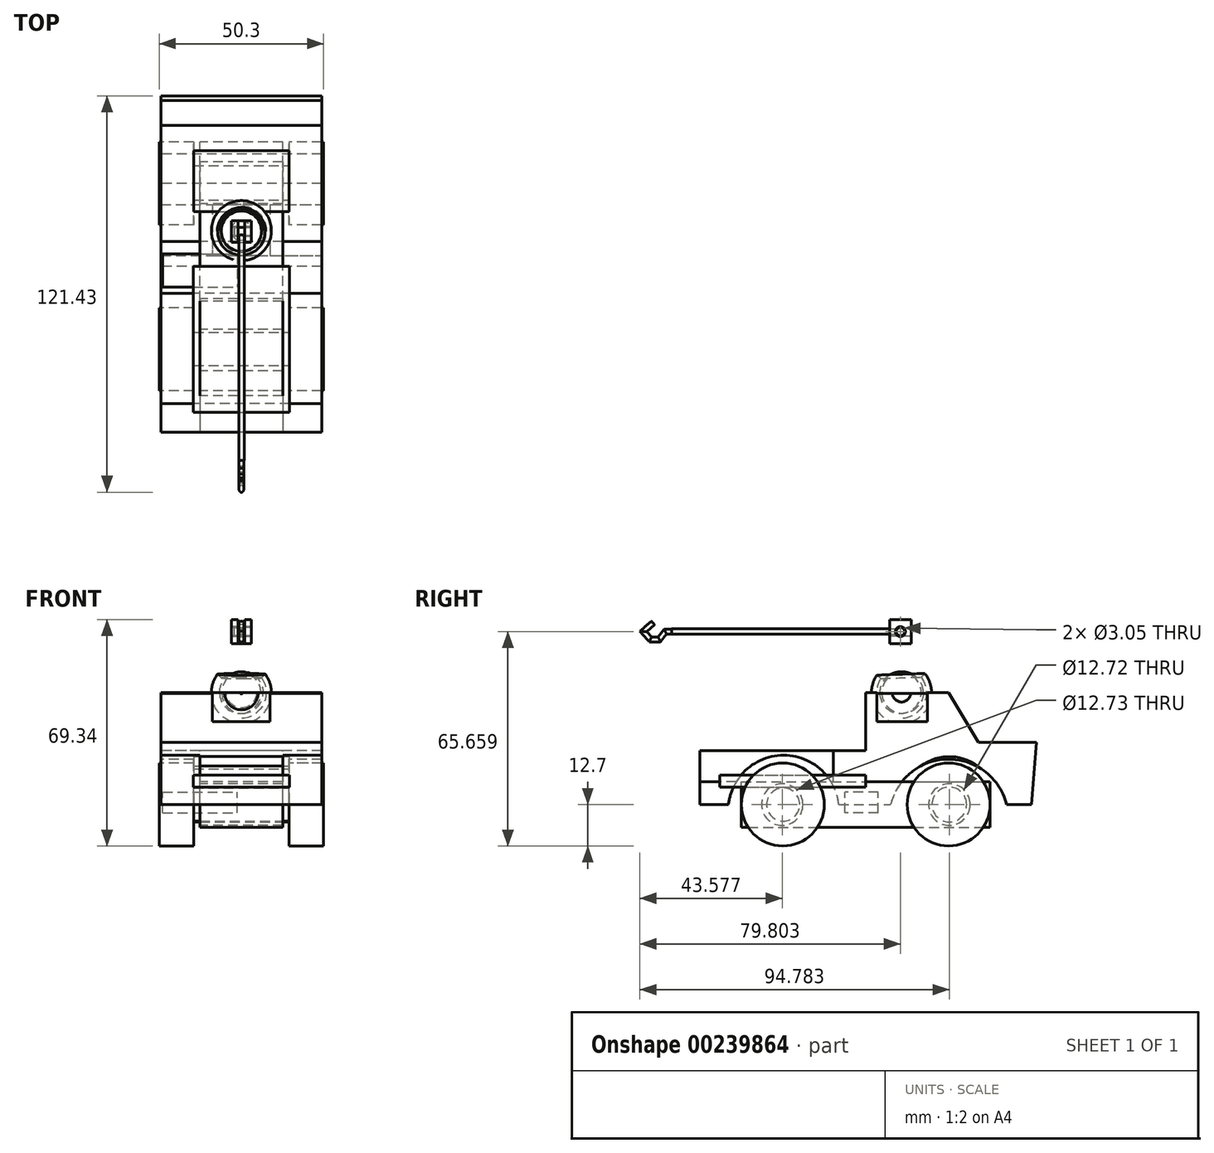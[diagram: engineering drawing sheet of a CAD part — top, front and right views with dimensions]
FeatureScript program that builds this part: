
annotation { "Feature Type Name" : "Feature", "Feature Type Description" : "" }
export const myFeature = defineFeature(function(context is Context, id is Id, definition is map)
    precondition{}
    {
        {
            var Q0;
            Q0=qCreatedBy(makeId("Right.planeOp"),FACE);
            var sketch = newSketch(context, id + "F0", { "sketchPlane" : qUnion([Q0])});
            skLineSegment(sketch, "E0", {"start": v(0, 0) * mm, "end": v(-50.8, 0) * mm, "construction": true});
            skLineSegment(sketch, "E1", {"start": v(0, 0) * mm, "end": v(50.8, 0) * mm, "construction": true});
            skCircle(sketch, "E2", {"center": v(-25.4, 0) * mm, "radius": 12.7 * mm});
            skCircle(sketch, "E3", {"center": v(25.4, 0) * mm, "radius": 12.7 * mm});
            skLineSegment(sketch, "E4", {"start": v(-42.06, 0) * mm, "end": v(-50.8, 0) * mm});
            skLineSegment(sketch, "E5", {"start": v(-50.8, 0) * mm, "end": v(-50.8, 16.51) * mm});
            skLineSegment(sketch, "E6", {"start": v(-50.8, 16.51) * mm, "end": v(0, 16.51) * mm});
            skLineSegment(sketch, "E7", {"start": v(0, 16.51) * mm, "end": v(0, 34.3) * mm});
            skLineSegment(sketch, "E8", {"start": v(0, 34.3) * mm, "end": v(25.4, 34.3) * mm});
            skLineSegment(sketch, "E9", {"start": v(25.4, 34.3) * mm, "end": v(34.47, 19) * mm});
            skLineSegment(sketch, "E10", {"start": v(34.47, 19) * mm, "end": v(52.25, 19) * mm});
            skLineSegment(sketch, "E11", {"start": v(52.25, 19) * mm, "end": v(50.8, 0) * mm});
            skArc(sketch, "E12", {"start": v(-8.23, 0) * mm, "mid": v(-25.15, 15.1) * mm, "end": v(-42.06, 0) * mm});
            skLineSegment(sketch, "E13", {"start": v(-8.23, 0) * mm, "end": v(7.62, 0) * mm});
            skArc(sketch, "E14", {"start": v(43.18, 0) * mm, "mid": v(25.4, 13.87) * mm, "end": v(7.62, 0) * mm});
            skLineSegment(sketch, "E15", {"start": v(43.18, 0) * mm, "end": v(50.8, 0) * mm});
            skSolve(sketch);
        }
        {
            var Q0;
            Q0=makeQuery(id+"F0.imprint","IMPRINT",FACE,{"disambiguationData":[TD([[makeQuery(id+"F0.imprint","IMPRINT",EDGE,{"derivedFrom":sQuery(id+"F0.wireOp",EDGE,"E4")}),-1.0]])]});
            extrude(context, id + "F1", {"entities" : qUnion([Q0]), "endBound" : BoundingType.SYMMETRIC, "depth" : 49.28 * mm});
        }
        {
            var Q0;
            Q0=makeQuery(id+"F0.imprint","IMPRINT",FACE,{"disambiguationData":[TD([[makeQuery(id+"F0.imprint","IMPRINT",EDGE,{"derivedFrom":sQuery(id+"F0.wireOp",EDGE,"E2")}),1.0]])]});
            var Q1;
            Q1=makeQuery(id+"F0.imprint","IMPRINT",FACE,{"disambiguationData":[TD([[makeQuery(id+"F0.imprint","IMPRINT",EDGE,{"derivedFrom":sQuery(id+"F0.wireOp",EDGE,"E3")}),1.0]])]});
            extrude(context, id + "F2", {"entities" : qUnion([Q0, Q1]), "endBound" : BoundingType.SYMMETRIC, "depth" : 50.3 * mm});
        }
        {
            var Q0;
            Q0=qCreatedBy(makeId("Right.planeOp"),FACE);
            var sketch = newSketch(context, id + "F3", { "sketchPlane" : qUnion([Q0])});
            skCircle(sketch, "E16", {"center": v(-25.3, 0) * mm, "radius": 14.08 * mm});
            skCircle(sketch, "E17", {"center": v(-25.3, 0) * mm, "radius": 5.07 * mm});
            skCircle(sketch, "E18", {"center": v(25.6, 0) * mm, "radius": 14.66 * mm});
            skCircle(sketch, "E19", {"center": v(25.6, 0) * mm, "radius": 5.32 * mm});
            skSolve(sketch);
        }
        {
            var Q0;
            Q0=makeQuery(id+"F3.imprint","IMPRINT",FACE,{"disambiguationData":[TD([[makeQuery(id+"F3.imprint","IMPRINT",EDGE,{"derivedFrom":sQuery(id+"F3.wireOp",EDGE,"E18")}),1.0]])]});
            extrude(context, id + "F4", {"entities" : qUnion([Q0]), "operationType" : NewBodyOperationType.REMOVE, "endBound" : BoundingType.SYMMETRIC, "oppositeDirection" : true, "depth" : 29.2 * mm});
        }
        {
            var Q0;
            Q0=makeQuery(id+"F3.imprint","IMPRINT",FACE,{"disambiguationData":[TD([[makeQuery(id+"F3.imprint","IMPRINT",EDGE,{"derivedFrom":sQuery(id+"F3.wireOp",EDGE,"E16")}),1.0]])]});
            extrude(context, id + "F5", {"entities" : qUnion([Q0]), "operationType" : NewBodyOperationType.REMOVE, "endBound" : BoundingType.SYMMETRIC, "oppositeDirection" : true, "depth" : 29.2 * mm});
        }
        {
            var Q0;
            Q0=makeQuery(id+"F1.opExtrude","SWEPT_FACE",FACE,{"disambiguationData":[OSD([sQuery(id+"F0.wireOp",EDGE,"E5")])]});
            var sketch = newSketch(context, id + "F6", { "sketchPlane" : qUnion([Q0])});
            skLineSegment(sketch, "E20.bottom", {"start": v(12.7, 6.99) * mm, "end": v(-12.7, 6.99) * mm});
            skLineSegment(sketch, "E20.top", {"start": v(12.7, 26.04) * mm, "end": v(-12.7, 26.04) * mm});
            skLineSegment(sketch, "E20.left", {"start": v(12.7, 6.99) * mm, "end": v(12.7, 26.04) * mm});
            skLineSegment(sketch, "E20.right", {"start": v(-12.7, 6.99) * mm, "end": v(-12.7, 26.04) * mm});
            skPoint(sketch, "E20.middle", {"position": v(0, 16.51) * mm});
            skSolve(sketch);
        }
        {
            var Q0;
            {var subQ0=sQuery(id+"F6.wireOp",EDGE,"E20.bottom");Q0=makeQuery(id+"F6.imprint","IMPRINT",FACE,{"disambiguationData":[TD([[makeQuery(id+"F6.imprint","IMPRINT",EDGE,{"derivedFrom":subQ0}),-1.0]])]});}
            extrude(context, id + "F7", {"entities" : qUnion([Q0]), "operationType" : NewBodyOperationType.REMOVE, "oppositeDirection" : true, "depth" : 40.9 * mm});
        }
        {
            var Q0;
            Q0=qCreatedBy(makeId("Front.planeOp"),FACE);
            var sketch = newSketch(context, id + "F8", { "sketchPlane" : qUnion([Q0])});
            skLineSegment(sketch, "E21.bottom", {"start": v(-14.78, 9) * mm, "end": v(14.78, 9) * mm});
            skLineSegment(sketch, "E21.top", {"start": v(-14.78, 5.33) * mm, "end": v(14.78, 5.33) * mm});
            skLineSegment(sketch, "E21.left", {"start": v(-14.78, 9) * mm, "end": v(-14.78, 5.33) * mm});
            skLineSegment(sketch, "E21.right", {"start": v(14.78, 9) * mm, "end": v(14.78, 5.33) * mm});
            skPoint(sketch, "E21.middle", {"position": v(0, 7.16) * mm});
            skSolve(sketch);
        }
        {
            var Q0;
            Q0 = qSketchRegion(id + "F8", true);
            extrude(context, id + "F9", {"entities" : qUnion([Q0]), "depth" : 44.7 * mm});
        }
        {
            var Q0;
            Q0=qCreatedBy(makeId("Right.planeOp"),FACE);
            var sketch = newSketch(context, id + "F10", { "sketchPlane" : qUnion([Q0])});
            skLineSegment(sketch, "E22.bottom", {"start": v(-38.1, -6.98) * mm, "end": v(38.1, -6.98) * mm});
            skLineSegment(sketch, "E22.top", {"start": v(-38.1, 6.98) * mm, "end": v(38.1, 6.98) * mm});
            skLineSegment(sketch, "E22.left", {"start": v(-38.1, -6.98) * mm, "end": v(-38.1, 6.98) * mm});
            skLineSegment(sketch, "E22.right", {"start": v(38.1, -6.98) * mm, "end": v(38.1, 6.98) * mm});
            skPoint(sketch, "E22.middle", {"position": v(0, 0) * mm});
            skCircle(sketch, "E23", {"center": v(25.6, 0) * mm, "radius": 6.36 * mm});
            skCircle(sketch, "E24", {"center": v(-25.6, 0) * mm, "radius": 6.36 * mm});
            skSolve(sketch);
        }
        {
            var Q0;
            Q0=makeQuery(id+"F10.imprint","IMPRINT",FACE,{"disambiguationData":[TD([[makeQuery(id+"F10.imprint","IMPRINT",EDGE,{"derivedFrom":sQuery(id+"F10.wireOp",EDGE,"E22.bottom")}),1.0]])]});
            extrude(context, id + "F11", {"entities" : qUnion([Q0]), "endBound" : BoundingType.SYMMETRIC, "depth" : 25.4 * mm});
        }
        {
            var Q0;
            Q0=qCreatedBy(makeId("Right.planeOp"),FACE);
            var sketch = newSketch(context, id + "F12", { "sketchPlane" : qUnion([Q0])});
            skCircle(sketch, "E25", {"center": v(11.28, 34.3) * mm, "radius": 9.53 * mm});
            skCircle(sketch, "E26", {"center": v(11.28, 34.3) * mm, "radius": 7.94 * mm});
            skCircle(sketch, "E27", {"center": v(11.28, 34.3) * mm, "radius": 6.35 * mm});
            skLineSegment(sketch, "E28", {"start": v(4.61, 38.6) * mm, "end": v(0, 42.52) * mm});
            skLineSegment(sketch, "E29", {"start": v(11.28, 34.3) * mm, "end": v(11.28, 27.94) * mm, "construction": true});
            skLineSegment(sketch, "E30", {"start": v(10.62, 43.8) * mm, "end": v(11.28, 24.77) * mm});
            skLineSegment(sketch, "E31.bottom", {"start": v(11.28, 34.3) * mm, "end": v(8.23, 34.3) * mm});
            skLineSegment(sketch, "E31.top", {"start": v(11.28, 49.53) * mm, "end": v(8.23, 49.53) * mm});
            skSolve(sketch);
        }
        {
            var Q0;
            Q0=makeQuery(id+"F1.opExtrude","CAP_FACE",FACE,{"disambiguationData":[OSD([sQuery(id+"F0.wireOp",EDGE,"E4"),sQuery(id+"F0.wireOp",EDGE,"E5"),sQuery(id+"F0.wireOp",EDGE,"E6"),sQuery(id+"F0.wireOp",EDGE,"E7"),sQuery(id+"F0.wireOp",EDGE,"E8"),sQuery(id+"F0.wireOp",EDGE,"E9"),sQuery(id+"F0.wireOp",EDGE,"E10"),sQuery(id+"F0.wireOp",EDGE,"E11"),sQuery(id+"F0.wireOp",EDGE,"E12"),sQuery(id+"F0.wireOp",EDGE,"E13"),sQuery(id+"F0.wireOp",EDGE,"E14"),sQuery(id+"F0.wireOp",EDGE,"E15")])],"isStart":false});
            var sketch = newSketch(context, id + "F13", { "sketchPlane" : qUnion([Q0])});
            skPoint(sketch, "E32.firstSnap0", {"position": v(0, 25.4) * mm});
            skLineSegment(sketch, "E32.bottom", {"start": v(3.35, 25.4) * mm, "end": v(18.9, 25.4) * mm});
            skLineSegment(sketch, "E32.top", {"start": v(3.35, 34.3) * mm, "end": v(18.9, 34.3) * mm});
            skLineSegment(sketch, "E32.left", {"start": v(3.35, 25.4) * mm, "end": v(3.35, 34.3) * mm});
            skLineSegment(sketch, "E32.right", {"start": v(18.9, 25.4) * mm, "end": v(18.9, 34.3) * mm});
            skSolve(sketch);
        }
        {
            var Q0;
            Q0=makeQuery(id+"F13.imprint","IMPRINT",FACE,{"disambiguationData":[TD([[makeQuery(id+"F13.imprint","IMPRINT",EDGE,{"derivedFrom":sQuery(id+"F13.wireOp",EDGE,"E32.bottom")}),1.0]])]});
            extrude(context, id + "F14", {"entities" : qUnion([Q0]), "operationType" : NewBodyOperationType.REMOVE, "oppositeDirection" : true, "depth" : 66.3 * mm});
        }
        {
            var Q0;
            {var subQ0=sQuery(id+"F12.wireOp",EDGE,"E30");var subQ1=sQuery(id+"F12.wireOp",EDGE,"E25");var subQ2=makeQuery(id+"F12.imprint","INTERSECT",VERTEX,{"disambiguationData":[OD(1.0)],"derivedFrom":[subQ1,subQ0]});Q0=makeQuery(id+"F12.imprint","IMPRINT",FACE,{"disambiguationData":[TD([[makeQuery(id+"F12.imprint","IMPRINT",EDGE,{"disambiguationData":[TD([[subQ2,1.0]])],"derivedFrom":subQ1}),1.0]])]});}
            var Q1;
            {var subQ0=sQuery(id+"F12.wireOp",EDGE,"E30");var subQ4=makeQuery(id+"F12.imprint","IMPRINT",VERTEX,{"derivedFrom":subQ0});Q1=makeQuery(id+"F12.imprint","IMPRINT",FACE,{"disambiguationData":[TD([[makeQuery(id+"F12.imprint","IMPRINT",EDGE,{"disambiguationData":[TD([[subQ4,1.0]])],"derivedFrom":subQ0}),-1.0]])]});}
            var Q2;
            Q2=sQuery(id+"F12.wireOp",EDGE,"E30");
            revolve(context, id + "F15", {"operationType" : NewBodyOperationType.ADD, "entities" : qUnion([Q0, Q1]), "axis" : qUnion([Q2]), "revolveType" : RevolveType.FULL});
        }
        {
            var Q0;
            Q0=qCreatedBy(makeId("Top.planeOp"),FACE);
            cPlane(context, id + "F16", {"entities" : qUnion([Q0]), "cplaneType" : CPlaneType.OFFSET, "offset" : 34.3 * mm, "width" : 152.4 * mm, "height" : 152.4 * mm});
        }
        {
            var Q0;
            Q0=qCreatedBy(id+"F16.planeOp",FACE);
            var sketch = newSketch(context, id + "F17", { "sketchPlane" : qUnion([Q0])});
            skCircle(sketch, "E33", {"center": v(0, 10.67) * mm, "radius": 2.6 * mm});
            skSolve(sketch);
        }
        {
            var Q0;
            Q0=sQuery(id+"F17.wireOp",EDGE,"E33");
            extrude(context, id + "F18", {"bodyType" : ToolBodyType.SURFACE, "surfaceEntities" : qUnion([Q0]), "depth" : 15.24 * mm});
        }
        {
            var Q0;
            Q0=qCreatedBy(id+"F16.planeOp",FACE);
            cPlane(context, id + "F19", {"entities" : qUnion([Q0]), "cplaneType" : CPlaneType.OFFSET, "offset" : 15 * mm, "width" : 152.4 * mm, "height" : 152.4 * mm});
        }
        {
            var Q0;
            Q0=qCreatedBy(id+"F19.planeOp",FACE);
            var sketch = newSketch(context, id + "F20", { "sketchPlane" : qUnion([Q0])});
            skLineSegment(sketch, "E34.bottom", {"start": v(-3.04, 13.92) * mm, "end": v(3.05, 13.92) * mm});
            skLineSegment(sketch, "E34.top", {"start": v(-3.04, 7.32) * mm, "end": v(3.05, 7.32) * mm});
            skLineSegment(sketch, "E34.left", {"start": v(-3.04, 13.92) * mm, "end": v(-3.04, 7.32) * mm});
            skLineSegment(sketch, "E34.right", {"start": v(3.05, 13.92) * mm, "end": v(3.05, 7.32) * mm});
            skLineSegment(sketch, "E35", {"start": v(-1.01, 13.92) * mm, "end": v(-1.01, 7.32) * mm});
            skLineSegment(sketch, "E36", {"start": v(1.02, 13.92) * mm, "end": v(1.02, 7.32) * mm});
            skSolve(sketch);
        }
        {
            var Q0;
            {var subQ0=sQuery(id+"F20.wireOp",EDGE,"E34.left");Q0=makeQuery(id+"F20.imprint","IMPRINT",FACE,{"disambiguationData":[TD([[makeQuery(id+"F20.imprint","IMPRINT",EDGE,{"derivedFrom":subQ0}),1.0]])]});}
            var Q1;
            {var subQ0=sQuery(id+"F20.wireOp",EDGE,"E34.right");Q1=makeQuery(id+"F20.imprint","IMPRINT",FACE,{"disambiguationData":[TD([[makeQuery(id+"F20.imprint","IMPRINT",EDGE,{"derivedFrom":subQ0}),-1.0]])]});}
            extrude(context, id + "F21", {"entities" : qUnion([Q0, Q1]), "depth" : 7.37 * mm});
        }
        {
            var Q0;
            Q0=makeQuery(id+"F21.opExtrude","SWEPT_FACE",FACE,{"disambiguationData":[OSD([sQuery(id+"F20.wireOp",EDGE,"E34.left")])]});
            var sketch = newSketch(context, id + "F22", { "sketchPlane" : qUnion([Q0])});
            skCircle(sketch, "E37", {"center": v(-10.62, 52.96) * mm, "radius": 1.52 * mm});
            skPoint(sketch, "E37.centerSnap0", {"position": v(-13.92, 52.96) * mm});
            skCircle(sketch, "E38", {"center": v(-10.62, 52.96) * mm, "radius": 1.27 * mm});
            skSolve(sketch);
        }
        {
            var Q0;
            Q0=makeQuery(id+"F22.imprint","IMPRINT",FACE,{"disambiguationData":[TD([[makeQuery(id+"F22.imprint","IMPRINT",EDGE,{"derivedFrom":sQuery(id+"F22.wireOp",EDGE,"E37")}),1.0]])]});
            extrude(context, id + "F23", {"entities" : qUnion([Q0]), "operationType" : NewBodyOperationType.REMOVE, "oppositeDirection" : true, "depth" : 29.72 * mm});
        }
        {
            var Q0;
            Q0=makeQuery(id+"F23.boolean.opBoolean","SPLIT",FACE,{"disambiguationData":[TD([makeQuery(id+"F23.opExtrude","SWEPT_FACE",FACE,{"disambiguationData":[OSD([sQuery(id+"F22.wireOp",EDGE,"E38")])]})])],"derivedFrom":makeQuery(id+"F21.opExtrude","SWEPT_FACE",FACE,{"disambiguationData":[OSD([sQuery(id+"F20.wireOp",EDGE,"E34.right")])]})});
            extrude(context, id + "F24", {"entities" : qUnion([Q0]), "oppositeDirection" : true, "depth" : 5.18 * mm});
        }
        {
            var Q0;
            {var subQ0=sQuery(id+"F20.wireOp",EDGE,"E35");Q0=makeQuery(id+"F20.imprint","IMPRINT",FACE,{"disambiguationData":[TD([[makeQuery(id+"F20.imprint","IMPRINT",EDGE,{"derivedFrom":subQ0}),1.0]])]});}
            extrude(context, id + "F25", {"entities" : qUnion([Q0]), "depth" : 2.3 * mm});
        }
        {
            var Q0;
            Q0=qCreatedBy(makeId("Front.planeOp"),FACE);
            cPlane(context, id + "F26", {"entities" : qUnion([Q0]), "cplaneType" : CPlaneType.OFFSET, "offset" : 10.4 * mm, "oppositeDirection" : true, "width" : 152.4 * mm, "height" : 152.4 * mm});
        }
        {
            var Q0;
            Q0=qCreatedBy(id+"F26.planeOp",FACE);
            var sketch = newSketch(context, id + "F27", { "sketchPlane" : qUnion([Q0])});
            skCircle(sketch, "E39", {"center": v(0, 52.97) * mm, "radius": 0.83 * mm});
            skSolve(sketch);
        }
        {
            var Q0;
            Q0 = qSketchRegion(id + "F27", true);
            extrude(context, id + "F28", {"entities" : qUnion([Q0]), "operationType" : NewBodyOperationType.ADD, "depth" : 69.85 * mm});
        }
        {
            var Q0;
            Q0=qCreatedBy(makeId("Right.planeOp"),FACE);
            var sketch = newSketch(context, id + "F29", { "sketchPlane" : qUnion([Q0])});
            skLineSegment(sketch, "E40", {"start": v(-58.77, 53) * mm, "end": v(-61.44, 53) * mm});
            skLineSegment(sketch, "E41", {"start": v(-61.44, 53) * mm, "end": v(-63.3, 50.61) * mm});
            skLineSegment(sketch, "E42", {"start": v(-63.3, 50.61) * mm, "end": v(-65.94, 50.61) * mm});
            skLineSegment(sketch, "E43", {"start": v(-65.94, 50.61) * mm, "end": v(-68.08, 53) * mm});
            skLineSegment(sketch, "E44", {"start": v(-68.08, 53) * mm, "end": v(-65.18, 55.6) * mm});
            skSolve(sketch);
        }
        {
            var Q0;
            Q0=makeQuery(id+"F28.opExtrude","CAP_FACE",FACE,{"disambiguationData":[OSD([sQuery(id+"F27.wireOp",EDGE,"E39")])],"isStart":false});
            var sketch = newSketch(context, id + "F30", { "sketchPlane" : qUnion([Q0])});
            skCircle(sketch, "E45", {"center": v(0, 52.97) * mm, "radius": 0.75 * mm});
            skSolve(sketch);
        }
        {
            var Q0;
            Q0=makeQuery(id+"F30.imprint","IMPRINT",FACE,{"disambiguationData":[TD([[makeQuery(id+"F30.imprint","IMPRINT",EDGE,{"derivedFrom":sQuery(id+"F30.wireOp",EDGE,"E45")}),1.0]])]});
            var Q1;
            Q1=sQuery(id+"F29.wireOp",EDGE,"E40");
            var Q2;
            Q2=sQuery(id+"F29.wireOp",EDGE,"E41");
            var Q3;
            Q3=sQuery(id+"F29.wireOp",EDGE,"E42");
            var Q4;
            Q4=sQuery(id+"F29.wireOp",EDGE,"E43");
            var Q5;
            Q5=sQuery(id+"F29.wireOp",EDGE,"E44");
            sweep(context, id + "F31", {"operationType" : NewBodyOperationType.ADD, "profiles" : qUnion([Q0]), "path" : qUnion([Q1, Q2, Q3, Q4, Q5])});
        }
        {
            var Q0;
            Q0=makeQuery(id+"F14.boolean.opBoolean","COPY",FACE,{"derivedFrom":makeQuery(id+"F14.opExtrude","SWEPT_FACE",FACE,{"disambiguationData":[OSD([sQuery(id+"F13.wireOp",EDGE,"E32.bottom")])]})});
            var sketch = newSketch(context, id + "F32", { "sketchPlane" : qUnion([Q0])});
            skLineSegment(sketch, "E46.bottom", {"start": v(-24.64, 18.9) * mm, "end": v(-8.83, 18.9) * mm});
            skLineSegment(sketch, "E46.top", {"start": v(-24.64, 3.35) * mm, "end": v(-8.83, 3.35) * mm});
            skLineSegment(sketch, "E46.left", {"start": v(-24.64, 18.9) * mm, "end": v(-24.64, 3.35) * mm});
            skLineSegment(sketch, "E46.right", {"start": v(-8.83, 18.9) * mm, "end": v(-8.83, 3.35) * mm});
            skLineSegment(sketch, "E47.bottom", {"start": v(24.64, 18.9) * mm, "end": v(8.75, 18.9) * mm});
            skLineSegment(sketch, "E47.top", {"start": v(24.64, 3.35) * mm, "end": v(8.75, 3.35) * mm});
            skLineSegment(sketch, "E47.left", {"start": v(24.64, 18.9) * mm, "end": v(24.64, 3.35) * mm});
            skLineSegment(sketch, "E47.right", {"start": v(8.75, 18.9) * mm, "end": v(8.75, 3.35) * mm});
            skSolve(sketch);
        }
        {
            var Q0;
            Q0=makeQuery(id+"F32.imprint","IMPRINT",FACE,{"disambiguationData":[TD([[makeQuery(id+"F32.imprint","IMPRINT",EDGE,{"derivedFrom":sQuery(id+"F32.wireOp",EDGE,"E46.bottom")}),-1.0]])]});
            var Q1;
            Q1=makeQuery(id+"F32.imprint","IMPRINT",FACE,{"disambiguationData":[TD([[makeQuery(id+"F32.imprint","IMPRINT",EDGE,{"derivedFrom":sQuery(id+"F32.wireOp",EDGE,"E47.bottom")}),-1.0]])]});
            extrude(context, id + "F33", {"entities" : qUnion([Q0, Q1]), "operationType" : NewBodyOperationType.ADD, "depth" : 8.64 * mm});
        }
        {
            var Q0;
            Q0=makeQuery(id+"F11.opExtrude","CAP_FACE",FACE,{"disambiguationData":[OSD([sQuery(id+"F10.wireOp",EDGE,"E22.bottom"),sQuery(id+"F10.wireOp",EDGE,"E22.top"),sQuery(id+"F10.wireOp",EDGE,"E22.left"),sQuery(id+"F10.wireOp",EDGE,"E22.right"),sQuery(id+"F10.wireOp",EDGE,"E23"),sQuery(id+"F10.wireOp",EDGE,"E24")])],"isStart":true});
            var sketch = newSketch(context, id + "F34", { "sketchPlane" : qUnion([Q0])});
            skLineSegment(sketch, "E48.bottom", {"start": v(-3.81, -2.54) * mm, "end": v(6.35, -2.54) * mm});
            skLineSegment(sketch, "E48.top", {"start": v(-3.81, 3.81) * mm, "end": v(6.35, 3.81) * mm});
            skLineSegment(sketch, "E48.left", {"start": v(-3.81, -2.54) * mm, "end": v(-3.81, 3.81) * mm});
            skLineSegment(sketch, "E48.right", {"start": v(6.35, -2.54) * mm, "end": v(6.35, 3.81) * mm});
            skSolve(sketch);
        }
        {
            var Q0;
            Q0=makeQuery(id+"F34.imprint","IMPRINT",FACE,{"disambiguationData":[TD([[makeQuery(id+"F34.imprint","IMPRINT",EDGE,{"derivedFrom":sQuery(id+"F34.wireOp",EDGE,"E48.bottom")}),1.0]])]});
            extrude(context, id + "F35", {"entities" : qUnion([Q0]), "endBound" : BoundingType.SYMMETRIC, "depth" : 22.86 * mm});
        }
    });
